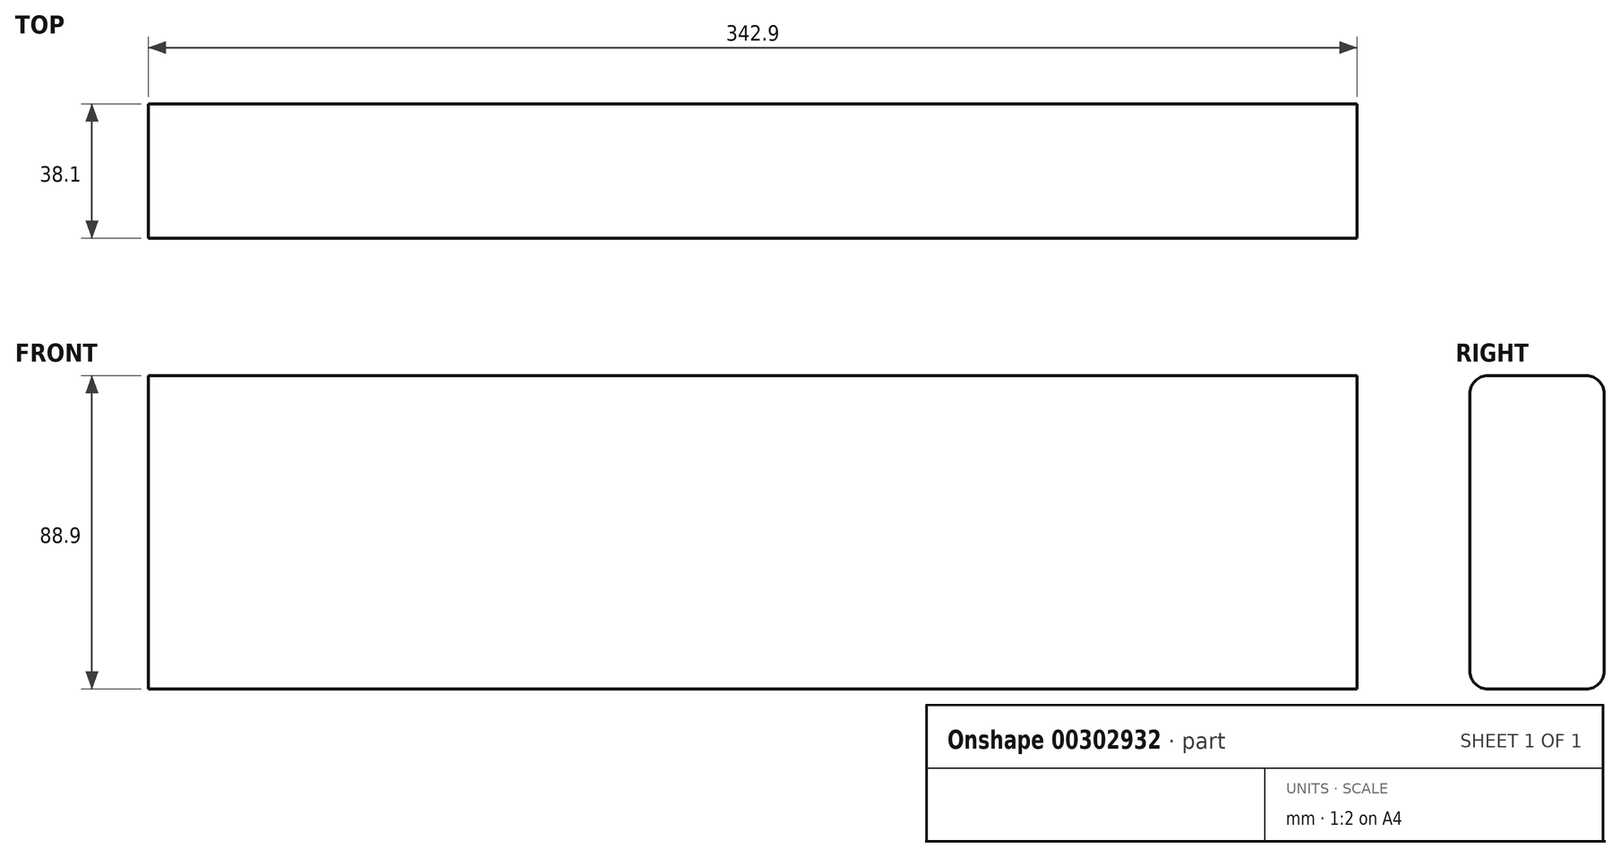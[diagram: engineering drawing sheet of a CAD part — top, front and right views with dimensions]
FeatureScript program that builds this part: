
annotation { "Feature Type Name" : "Feature", "Feature Type Description" : "" }
export const myFeature = defineFeature(function(context is Context, id is Id, definition is map)
    precondition{}
    {
        {
            var Q0;
            Q0=qCreatedBy(makeId("Front.planeOp"),FACE);
            var sketch = newSketch(context, id + "F0", { "sketchPlane" : qUnion([Q0])});
            skLineSegment(sketch, "E0.bottom", {"start": v(171.45, -44.45) * mm, "end": v(-171.45, -44.45) * mm});
            skLineSegment(sketch, "E0.top", {"start": v(171.45, 44.45) * mm, "end": v(-171.45, 44.45) * mm});
            skLineSegment(sketch, "E0.left", {"start": v(171.45, -44.45) * mm, "end": v(171.45, 44.45) * mm});
            skLineSegment(sketch, "E0.right", {"start": v(-171.45, -44.45) * mm, "end": v(-171.45, 44.45) * mm});
            skPoint(sketch, "E0.middle", {"position": v(0, 0) * mm});
            skSolve(sketch);
        }
        {
            var Q0;
            Q0=qSketchRegion(id+"F0",true);
            extrude(context, id + "F1", {"entities" : qUnion([Q0]), "endBound" : BoundingType.SYMMETRIC, "depth" : 38.1 * mm});
        }
        {
            var Q0;
            Q0=makeQuery(id+"F1.opExtrude","CAP_EDGE",EDGE,{"disambiguationData":[OSD([sQuery(id+"F0.wireOp",EDGE,"E0.top")])],"isStart":false});
            var Q1;
            Q1=makeQuery(id+"F1.opExtrude","CAP_EDGE",EDGE,{"disambiguationData":[OSD([sQuery(id+"F0.wireOp",EDGE,"E0.top")])],"isStart":true});
            var Q2;
            Q2=makeQuery(id+"F1.opExtrude","CAP_EDGE",EDGE,{"disambiguationData":[OSD([sQuery(id+"F0.wireOp",EDGE,"E0.bottom")])],"isStart":true});
            var Q3;
            Q3=makeQuery(id+"F1.opExtrude","CAP_EDGE",EDGE,{"disambiguationData":[OSD([sQuery(id+"F0.wireOp",EDGE,"E0.bottom")])],"isStart":false});
            fillet(context, id + "F2", {"entities" : qUnion([Q0, Q1, Q2, Q3]), "radius" : 5.08 * mm, "tangentPropagation" : true, "allowEdgeOverflow" : false});
        }
    });
